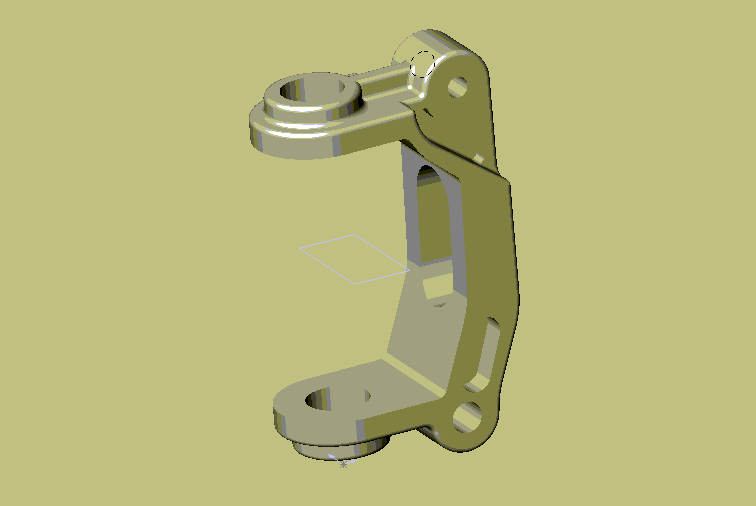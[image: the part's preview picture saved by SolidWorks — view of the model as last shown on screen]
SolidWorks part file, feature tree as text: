
SOLIDWORKS PART (.sldprt)
format: sldprt  version: not decoded by parser v0  size: 543,744 bytes
history: native  units: mm
features: sketch x11, cut_extrude x7, extrude x5, plane x4, fillet x4, material x1, mirror x1, hole x1, thread x1 (+8 scaffold rows collapsed)
feature tree (43):
  scaffold x8  (default folders/planes/origin — collapsed)
  material  "Matériau <non spécifié>"
  plane  "Plane1"
  plane  "Plane2"
  plane  "Plane3"
  sketch  "Esquisse1"  dims[D1=12.0mm D3=12.0mm D2=17.0mm]
  extrude  "Base-Extrusion"  Depth=42mm
  sketch  "Esquisse2"  dims[c1.D1=7.0mm c1.D2=8.0mm c1.D11=14.0mm c2.D2=4.0mm c2.D9=3.5mm c2.D12=10.0mm c2.D3=4.0mm c2.D4=2.5mm c2.D5=10.0mm c2.D6=13.0mm c2.D7=31.0mm c2.D8=4.0mm c3.D9=2.5mm c3.D10=2.5mm c3.D2=7.0mm]
  cut_extrude  "Enlèv. mat.-Extru.1"  [1 undecoded]
  sketch  "Esquisse3"  dims[D1=11.0mm]
  cut_extrude  "Enlèv. mat.-Extru.2"  Depth=2.5mm
  mirror  "Symétrie2"
  sketch  "Esquisse4"
  cut_extrude  "Enlèv. mat.-Extru.3"  Depth=1.5mm
  fillet  "Congé1"  Radius=1mm
  sketch  "Esquisse6"  dims[D2=4.5mm D1=8.0mm D3=2.0mm]
  extrude  "Boss.-Extru.1"  Depth=2mm
  extrude  "Congé2"  Depth=0.5mm
  plane  "Plan1"  Offset=15.5mm
  fillet  "Symétrie3"  [1 undecoded]
  extrude  "Congé3"  Depth=0.5mm
  sketch  "Esquisse7"  dims[D1=6.0mm]
  cut_extrude  "Enlèv. mat.-Extru.4"  [1 undecoded]
  sketch  "Esquisse8"  dims[D1=3.0mm D2=3.0mm]
  cut_extrude  "Enlèv. mat.-Extru.5"  Depth=2.5mm
  fillet  "Symétrie4"  [1 undecoded]
  sketch  "Esquisse12"  dims[D1=3.0mm]
  cut_extrude  "Enlèv. mat.-Extru.6"  [1 undecoded]
  hole  "Perçage2"  Diameter=2.05mm Depth=9.5mm
  sketch  "Esquisse14"
  sketch  "Esquisse13"  dims[hole-wizard template sketch: 59 standard entries collapsed; hole parameters kept: c18.Diamètre du perçage jusqu'au prochain=2.05mm c18.Profondeur du perçage jusqu'au prochain=9.5mm]
  thread  "Représentation de filetage2"  Diameter=5mm  [1 undecoded]
  fillet  "Symétrie5"  [1 undecoded]
  extrude  "Congé4"  Depth=0.5mm
  sketch  "Esquisse15"  dims[D1=3.25mm D3=3.25mm D2=9.0mm D4=7.0mm]
  cut_extrude  "Enlèv. mat.-Extru.7"  Depth=52.5mm
decode coverage: 21 of 30 modeling features carry decoded parameters
note: ~ marks probable driven/reference dimensions
note: 7 parameter values undecoded
summary: no parameter record found for 6 features
note: suppression state not decoded; provenance and decode notes live in map.json
